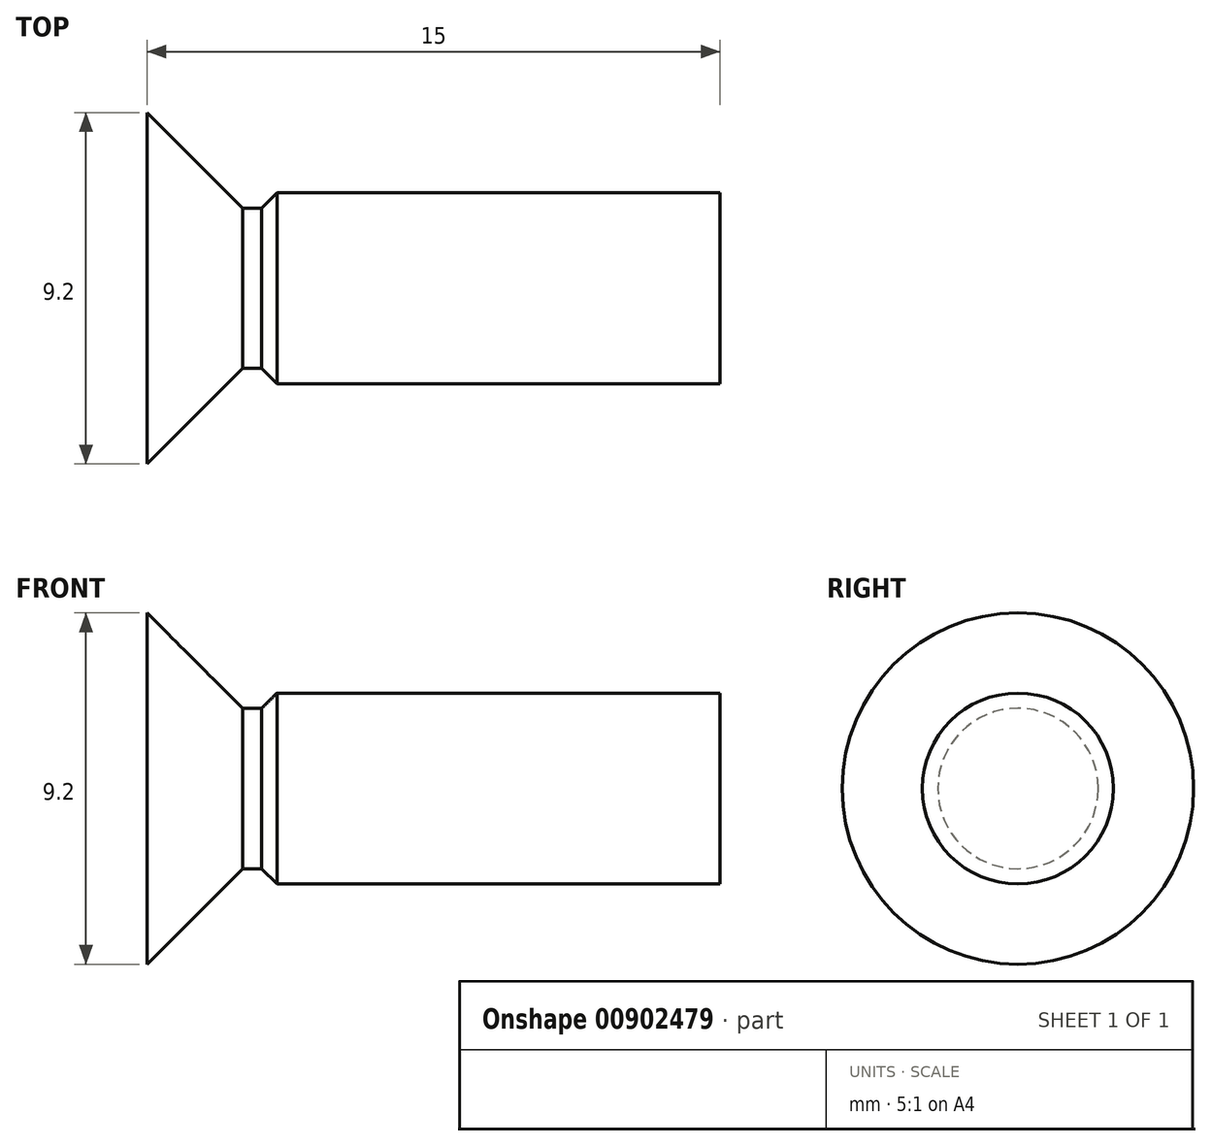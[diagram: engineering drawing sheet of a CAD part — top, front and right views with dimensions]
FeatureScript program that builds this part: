
annotation { "Feature Type Name" : "Feature", "Feature Type Description" : "" }
export const myFeature = defineFeature(function(context is Context, id is Id, definition is map)
    precondition{}
    {
        {
            var Q0;
            Q0=qCreatedBy(makeId("Front.planeOp"),FACE);
            var sketch = newSketch(context, id + "F0", { "sketchPlane" : qUnion([Q0])});
            skLineSegment(sketch, "E0.right", {"start": v(15, 0) * mm, "end": v(15, 2.5) * mm});
            skLineSegment(sketch, "E1", {"start": v(2.5, 2.1) * mm, "end": v(0, 4.6) * mm});
            skLineSegment(sketch, "E2", {"start": v(0, 4.6) * mm, "end": v(0, 0) * mm});
            skLineSegment(sketch, "E3", {"start": v(2.5, 2.1) * mm, "end": v(3, 2.1) * mm});
            skLineSegment(sketch, "E4", {"start": v(3, 2.1) * mm, "end": v(3.4, 2.5) * mm});
            skLineSegment(sketch, "E5", {"start": v(3.4, 2.5) * mm, "end": v(15, 2.5) * mm});
            skLineSegment(sketch, "E6", {"start": v(0, 0) * mm, "end": v(15, 0) * mm});
            skSolve(sketch);
        }
        {
            var Q0;
            Q0=makeQuery(id+"F0.imprint","IMPRINT",FACE,{"disambiguationData":[TD([[makeQuery(id+"F0.imprint","IMPRINT",EDGE,{"derivedFrom":sQuery(id+"F0.wireOp",EDGE,"E0.right")}),1.0]])]});
            var Q1;
            Q1=sQuery(id+"F0.wireOp",EDGE,"E6");
            revolve(context, id + "F1", {"surfaceOperationType" : NewSurfaceOperationType.NEW, "entities" : qUnion([Q0]), "axis" : qUnion([Q1]), "revolveType" : RevolveType.FULL});
        }
    });
